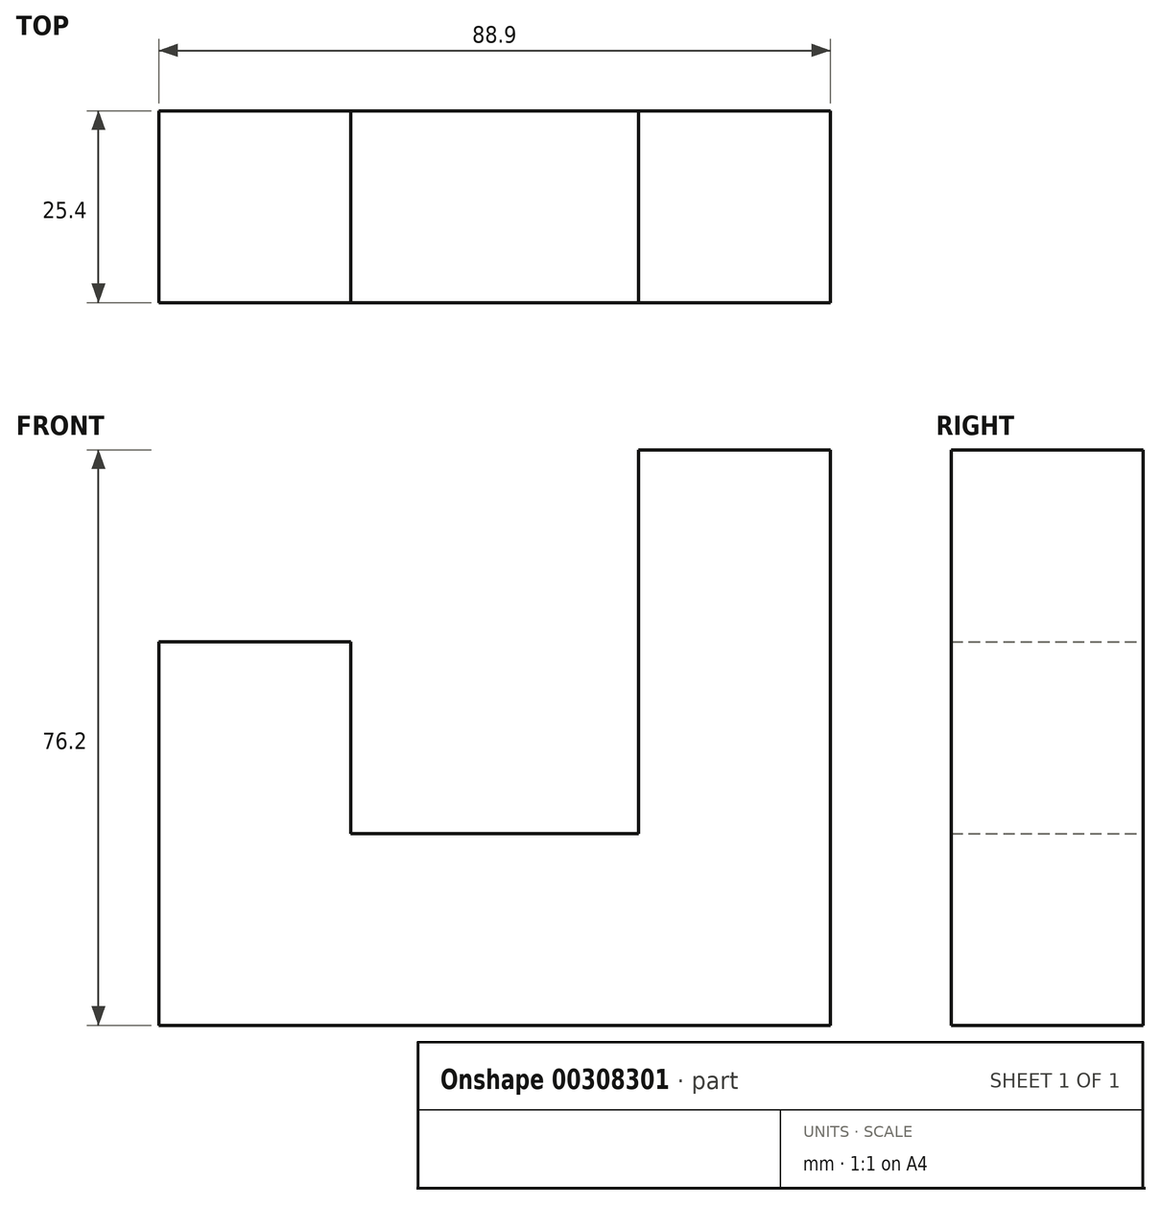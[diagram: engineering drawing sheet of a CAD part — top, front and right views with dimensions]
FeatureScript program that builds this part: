
annotation { "Feature Type Name" : "Feature", "Feature Type Description" : "" }
export const myFeature = defineFeature(function(context is Context, id is Id, definition is map)
    precondition{}
    {
        {
            var Q0;
            Q0=qCreatedBy(makeId("Front.planeOp"),FACE);
            var sketch = newSketch(context, id + "F0", { "sketchPlane" : qUnion([Q0])});
            skLineSegment(sketch, "E0", {"start": v(-44.36, -38.67) * mm, "end": v(44.54, -38.67) * mm});
            skLineSegment(sketch, "E1", {"start": v(44.54, -38.67) * mm, "end": v(44.54, 37.53) * mm});
            skLineSegment(sketch, "E2", {"start": v(44.54, 37.53) * mm, "end": v(19.14, 37.53) * mm});
            skLineSegment(sketch, "E3", {"start": v(19.14, 37.53) * mm, "end": v(19.14, -13.27) * mm});
            skLineSegment(sketch, "E4", {"start": v(19.14, -13.27) * mm, "end": v(-18.96, -13.27) * mm});
            skLineSegment(sketch, "E5", {"start": v(-18.96, -13.27) * mm, "end": v(-18.96, 12.13) * mm});
            skLineSegment(sketch, "E6", {"start": v(-18.96, 12.13) * mm, "end": v(-44.36, 12.13) * mm});
            skLineSegment(sketch, "E7", {"start": v(-44.36, 12.13) * mm, "end": v(-44.36, -38.67) * mm});
            skSolve(sketch);
        }
        {
            var Q0;
            Q0=makeQuery(id+"F0.imprint","IMPRINT",FACE,{"disambiguationData":[TD([[makeQuery(id+"F0.imprint","IMPRINT",EDGE,{"derivedFrom":sQuery(id+"F0.wireOp",EDGE,"E0")}),1.0]])]});
            extrude(context, id + "F1", {"entities" : qUnion([Q0]), "depth" : 25.4 * mm});
        }
    });
